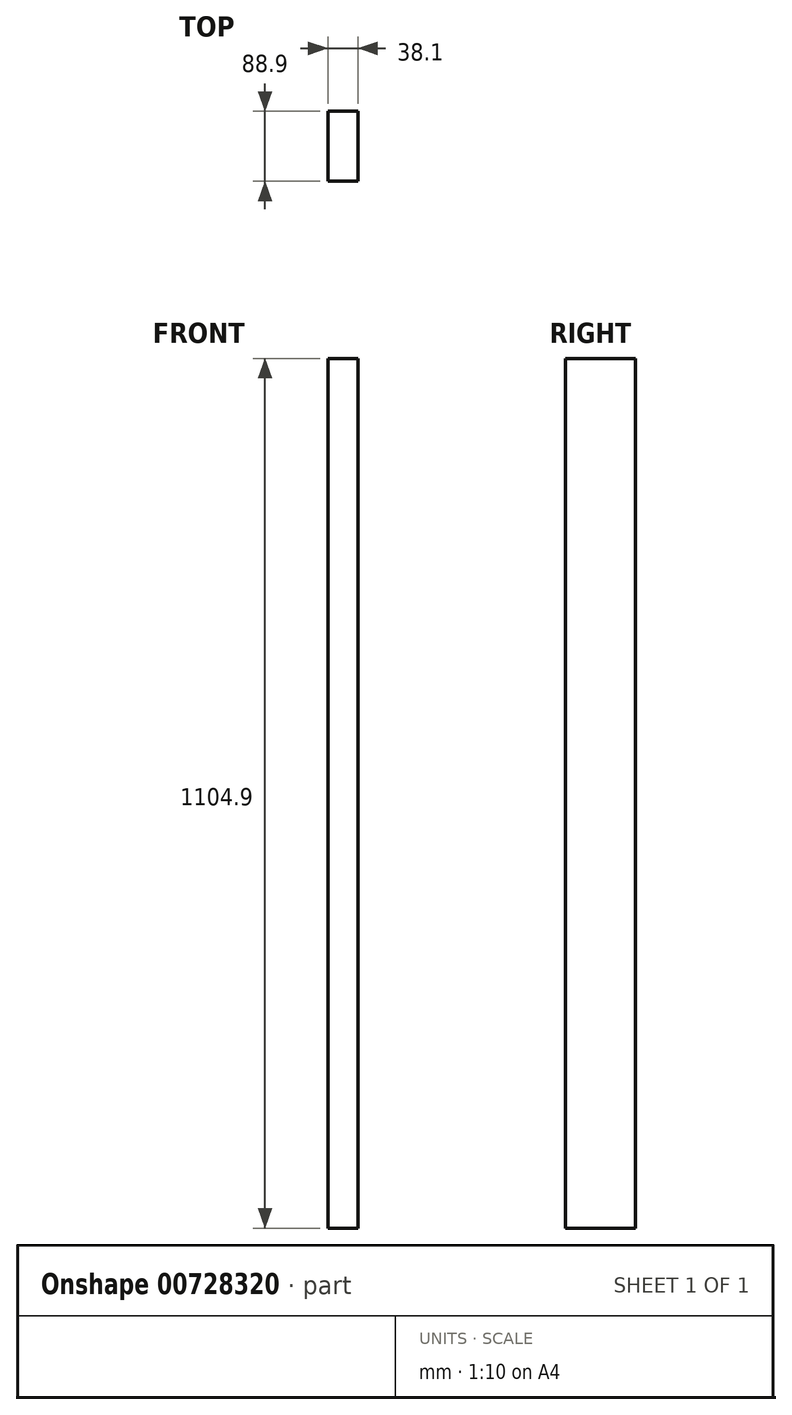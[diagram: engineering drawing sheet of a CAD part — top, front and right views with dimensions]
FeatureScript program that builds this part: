
annotation { "Feature Type Name" : "Feature", "Feature Type Description" : "" }
export const myFeature = defineFeature(function(context is Context, id is Id, definition is map)
    precondition{}
    {
        {
            var Q0;
            Q0=qCreatedBy(makeId("Front.planeOp"),FACE);
            var sketch = newSketch(context, id + "F0", { "sketchPlane" : qUnion([Q0])});
            skLineSegment(sketch, "E0.bottom", {"start": v(-19.05, -552.45) * mm, "end": v(19.05, -552.45) * mm});
            skLineSegment(sketch, "E0.top", {"start": v(-19.05, 552.45) * mm, "end": v(19.05, 552.45) * mm});
            skLineSegment(sketch, "E0.left", {"start": v(-19.05, -552.45) * mm, "end": v(-19.05, 552.45) * mm});
            skLineSegment(sketch, "E0.right", {"start": v(19.05, -552.45) * mm, "end": v(19.05, 552.45) * mm});
            skPoint(sketch, "E0.middle", {"position": v(0, 0) * mm});
            skSolve(sketch);
        }
        {
            var Q0;
            Q0=qSketchRegion(id+"F0",true);
            extrude(context, id + "F1", {"entities" : qUnion([Q0]), "depth" : 88.9 * mm});
        }
    });
